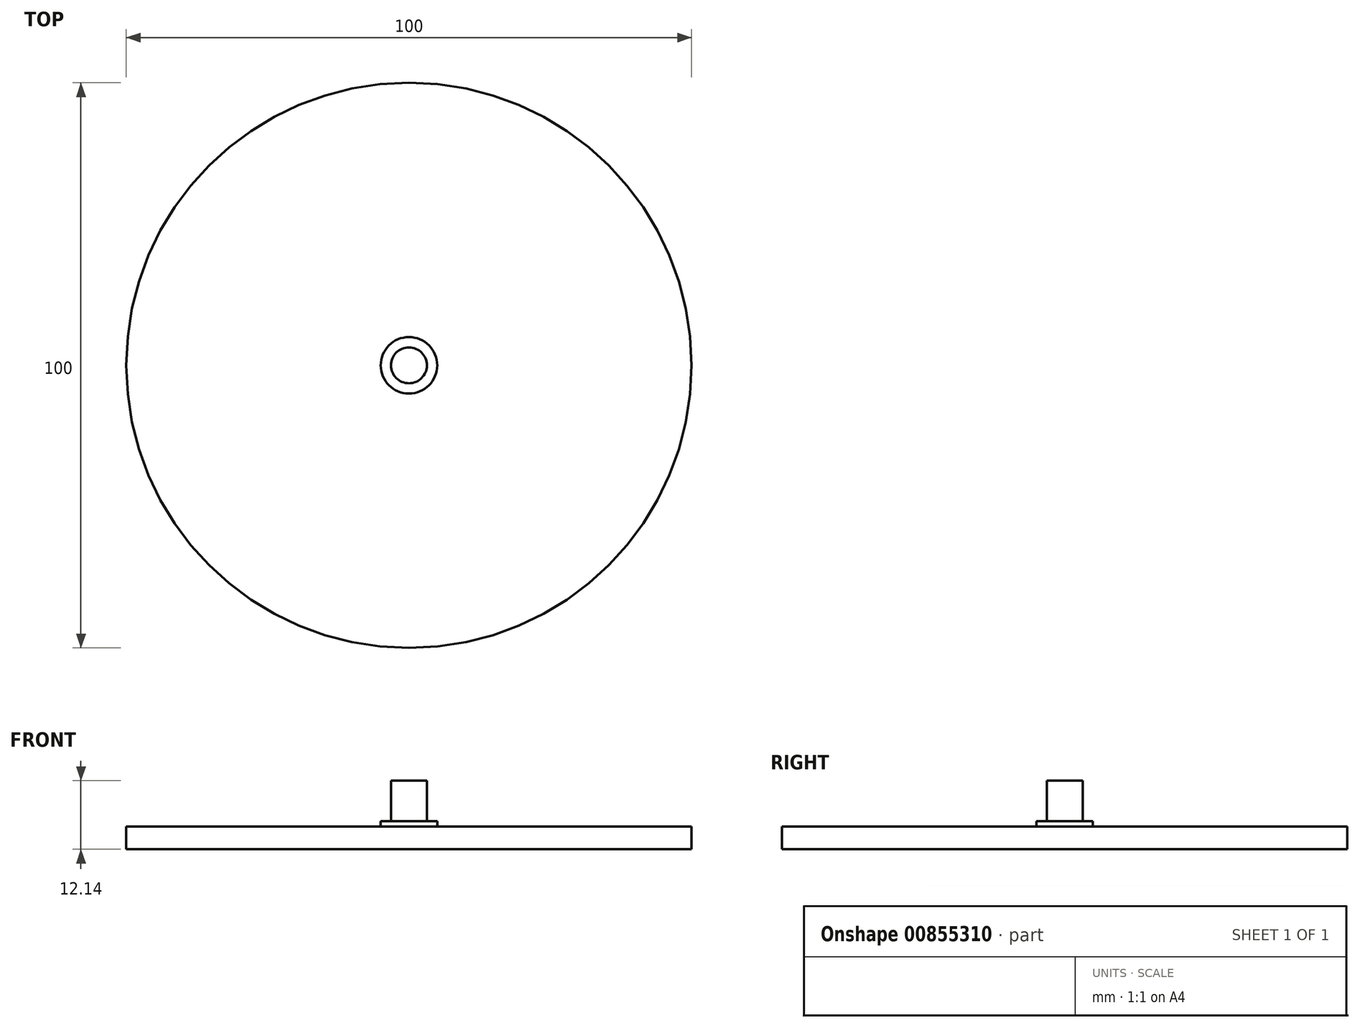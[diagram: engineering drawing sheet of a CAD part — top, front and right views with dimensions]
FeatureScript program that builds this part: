
annotation { "Feature Type Name" : "Feature", "Feature Type Description" : "" }
export const myFeature = defineFeature(function(context is Context, id is Id, definition is map)
    precondition{}
    {
        {
            var Q0;
            Q0=qCreatedBy(makeId("Top.planeOp"),FACE);
            var sketch = newSketch(context, id + "F0", { "sketchPlane" : qUnion([Q0])});
            skCircle(sketch, "E0", {"center": v(0, 0) * mm, "radius": 3.17 * mm});
            skCircle(sketch, "E1", {"center": v(0, 0) * mm, "radius": 5 * mm});
            skCircle(sketch, "E2", {"center": v(0, 0) * mm, "radius": 50 * mm});
            skSolve(sketch);
        }
        {
            var Q0;
            Q0=makeQuery(id+"F0.imprint","IMPRINT",FACE,{"disambiguationData":[TD([[makeQuery(id+"F0.imprint","IMPRINT",EDGE,{"derivedFrom":sQuery(id+"F0.wireOp",EDGE,"E0")}),-1.0]])]});
            var Q1;
            Q1=makeQuery(id+"F0.imprint","IMPRINT",FACE,{"disambiguationData":[TD([[makeQuery(id+"F0.imprint","IMPRINT",EDGE,{"derivedFrom":sQuery(id+"F0.wireOp",EDGE,"E0")}),1.0]])]});
            extrude(context, id + "F1", {"entities" : qUnion([Q0, Q1]), "depth" : 1 * mm, "offsetDistance" : 25 * mm});
        }
        {
            var Q0;
            Q0=makeQuery(id+"F1.opExtrude","CAP_FACE",FACE,{"disambiguationData":[OSD([sQuery(id+"F0.wireOp",EDGE,"E1")])],"isStart":false});
            var sketch = newSketch(context, id + "F2", { "sketchPlane" : qUnion([Q0])});
            skCircle(sketch, "E3", {"center": v(0, 0) * mm, "radius": 3.17 * mm});
            skSolve(sketch);
        }
        {
            var Q0;
            Q0=makeQuery(id+"F2.imprint","IMPRINT",FACE,{"disambiguationData":[TD([[makeQuery(id+"F2.imprint","IMPRINT",EDGE,{"derivedFrom":sQuery(id+"F2.wireOp",EDGE,"E3")}),1.0]])]});
            extrude(context, id + "F3", {"entities" : qUnion([Q0]), "operationType" : NewBodyOperationType.ADD, "depth" : 7.14 * mm, "offsetDistance" : 25 * mm});
        }
        {
            var Q0;
            Q0=makeQuery(id+"F0.imprint","IMPRINT",FACE,{"disambiguationData":[TD([[makeQuery(id+"F0.imprint","IMPRINT",EDGE,{"derivedFrom":sQuery(id+"F0.wireOp",EDGE,"E1")}),-1.0]])]});
            var Q1;
            Q1=makeQuery(id+"F1.opExtrude","CAP_FACE",FACE,{"disambiguationData":[OSD([sQuery(id+"F0.wireOp",EDGE,"E1")])],"isStart":true});
            extrude(context, id + "F4", {"entities" : qUnion([Q0, Q1]), "operationType" : NewBodyOperationType.ADD, "oppositeDirection" : true, "depth" : 4 * mm, "offsetDistance" : 25 * mm});
        }
    });
